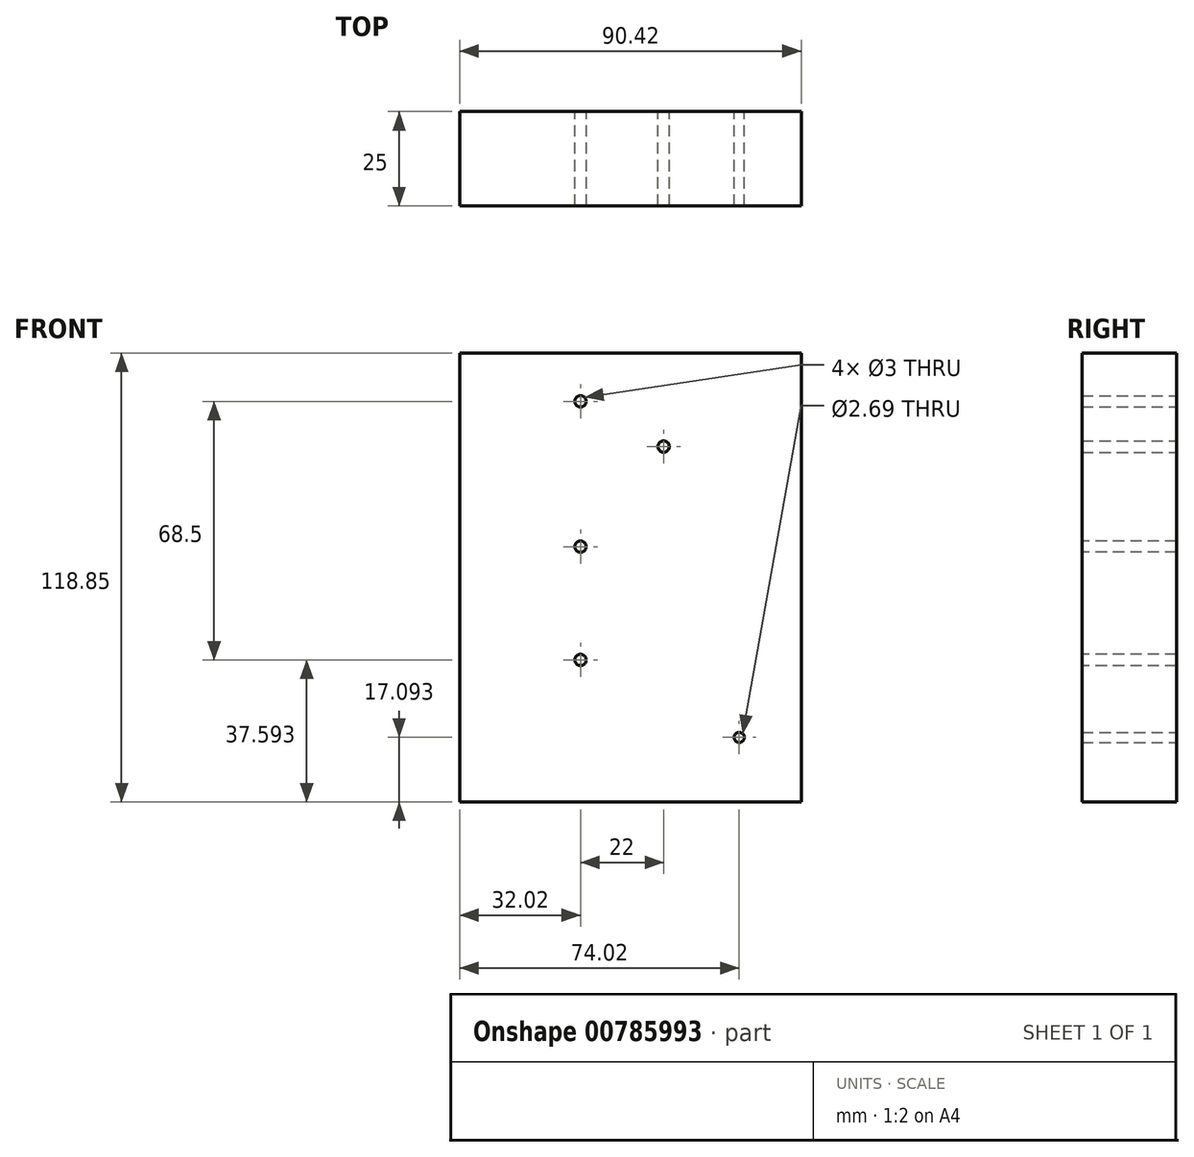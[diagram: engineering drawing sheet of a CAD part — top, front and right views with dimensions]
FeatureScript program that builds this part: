
annotation { "Feature Type Name" : "Feature", "Feature Type Description" : "" }
export const myFeature = defineFeature(function(context is Context, id is Id, definition is map)
    precondition{}
    {
        {
            var Q0;
            Q0=qCreatedBy(makeId("Front.planeOp"),FACE);
            var sketch = newSketch(context, id + "F0", { "sketchPlane" : qUnion([Q0])});
            skPoint(sketch, "E0.middle", {"position": v(0, 0) * mm});
            skCircle(sketch, "E1", {"center": v(0, -3.56) * mm, "radius": 1.5 * mm});
            skCircle(sketch, "E2", {"center": v(22, -15.56) * mm, "radius": 1.5 * mm});
            skCircle(sketch, "E3", {"center": v(42, -92.56) * mm, "radius": 1.34 * mm});
            skLineSegment(sketch, "E4.bottom", {"start": v(-32.02, 9.2) * mm, "end": v(58.4, 9.2) * mm});
            skLineSegment(sketch, "E4.top", {"start": v(-32.02, -109.65) * mm, "end": v(58.4, -109.65) * mm});
            skLineSegment(sketch, "E4.left", {"start": v(-32.02, 9.2) * mm, "end": v(-32.02, -109.65) * mm});
            skLineSegment(sketch, "E4.right", {"start": v(58.4, 9.2) * mm, "end": v(58.4, -109.65) * mm});
            skSolve(sketch);
        }
        {
            var Q0;
            Q0=qSketchRegion(id+"F0",true);
            extrude(context, id + "F1", {"entities" : qUnion([Q0]), "depth" : 25 * mm, "offsetDistance" : 25 * mm});
        }
        {
            var Q0;
            Q0=makeQuery(id+"F1.opExtrude","CAP_FACE",FACE,{"disambiguationData":[OSD([sQuery(id+"F0.wireOp",EDGE,"E1"),sQuery(id+"F0.wireOp",EDGE,"E2"),sQuery(id+"F0.wireOp",EDGE,"jtgmJv0B-tQnr-EZPJ-G5je-2fYfRnU7gmt3"),sQuery(id+"F0.wireOp",EDGE,"t2BzU8Tg-7VNa-X8mq-rHrr-yJKCZTptws2O"),sQuery(id+"F0.wireOp",EDGE,"E3"),sQuery(id+"F0.wireOp",EDGE,"E4.bottom"),sQuery(id+"F0.wireOp",EDGE,"E4.top"),sQuery(id+"F0.wireOp",EDGE,"E4.left"),sQuery(id+"F0.wireOp",EDGE,"E4.right")])],"isStart":false});
            var sketch = newSketch(context, id + "F2", { "sketchPlane" : qUnion([Q0])});
            skCircle(sketch, "E5", {"center": v(0, -42.06) * mm, "radius": 1.5 * mm});
            skCircle(sketch, "E6", {"center": v(0, -72.06) * mm, "radius": 1.5 * mm});
            skSolve(sketch);
        }
        {
            var Q0;
            Q0=qSketchRegion(id+"F2",true);
            extrude(context, id + "F3", {"entities" : qUnion([Q0]), "operationType" : NewBodyOperationType.REMOVE, "oppositeDirection" : true, "depth" : 25 * mm, "offsetDistance" : 25 * mm});
        }
    });
